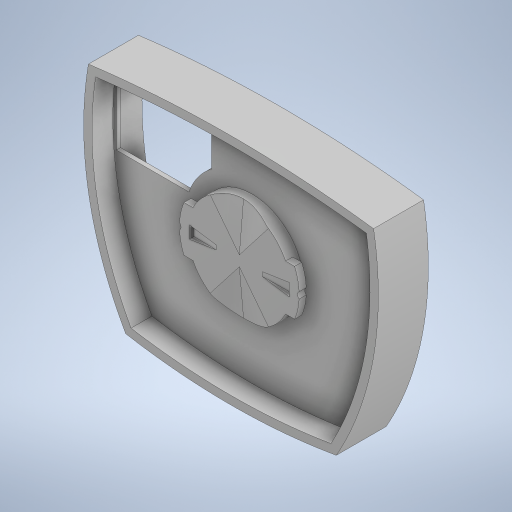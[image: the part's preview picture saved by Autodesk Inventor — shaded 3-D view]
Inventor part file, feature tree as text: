
AUTODESK INVENTOR PART (.ipt)
format: ipt  version: 2023 (Build 270158000, 158)  size: 479,744 bytes
history: mixed  units: in
note: dims shown in document units (in); Inventor stores cm internally (conversion verified against a paired STEP export)
features: extrude x14, sketch x8, projected_geometry x1, imported_body x1
ambient origin geometry x8: Origin, YZ Plane, XZ Plane, XY Plane, X Axis, Y Axis, Z Axis, Center Point
bodies: Solid1 (imported_parasolid), Body1 (imported_parasolid)
feature tree (24):
  extrude  "Extrusion5"  Depth=0.3937in
  sketch  "Sketch5"  dims[d13=0.9843in d18=2.5591in]
  extrude  "Extrusion6"  Depth=2.5591in
  extrude  "Extrusion7"  Depth=0.0787in
  extrude  "Extrusion8"  Depth=1.2795in
  extrude  "Extrusion9"  Depth=0.0787in
  sketch  "Sketch7"  dims[d21=1.2795in d22=1.2795in]
  extrude  "Extrusion10"  Depth=1.8898in
  extrude  "Extrusion12"  Depth=0.2756in TaperAngle=0.0deg
  extrude  "Extrusion14"  Depth=0.2362in
  extrude  "Extrusion15"  Depth=0.3937in TaperAngle=0.0deg
  extrude  "Extrusion16"  Depth=2.0315in
  extrude  "Extrusion17"  Depth=1.6535in
  extrude  "Extrusion18"  Depth=0.0787in
  extrude  "Extrusion19"  Depth=0.0787in
  extrude  "Extrusion20"  Depth=0.0787in
  sketch  "Sketch1"  dims[d10=0.3937in d11=0.0in d12=0.9055in]
  sketch  "Sketch6"  dims[d19=0.0787in d20=0.0787in]
  sketch  "Sketch8"  dims[d23=0.0787in d24=0.0787in]
  sketch  "Sketch10"  dims[d25=2.5591in d26=1.8898in]
  sketch  "Sketch11"  dims[d27=0.0787in d28=0.0in d29=0.2756in d30=0.0in]
  projected_geometry  "Projected Loop1"
  sketch  "Sketch12"  dims[d31=0.6693in d32=0.0in d33=1.2598in d36=0.3937in d37=0.0in d39=2.0315in d40=1.6535in d41=0.0787in d42=0.0787in d44=0.0787in d50=0.2756in d51=0.0in d54=0.0787in d55=0.0in d66=0.1969in d67=0.0709in d68=0.1969in d69=0.0709in d70=0.2362in d71=0.0in d72=0.2362in d73=0.0in d74=0.1181in d75=0.1181in d76=0.1969in d77=0.1181in d78=0.1969in d79=0.1181in d80=0.1969in d81=0.0in d82=0.1969in d83=0.0in d84=0.1181in d85=0.0in d86=0.0in d87=0.0in d88=0.0787in d89=0.0787in d90=0.2362in d91=0.0in d0=0.0197in d1=1.9685in d2=0.0197in d3=1.9685in]
  imported_body  NMx_Import_Brep_tag  [imported B-rep: ~43 faces, bbox_mm=[68.464898, 51.606881, 12.0]]
